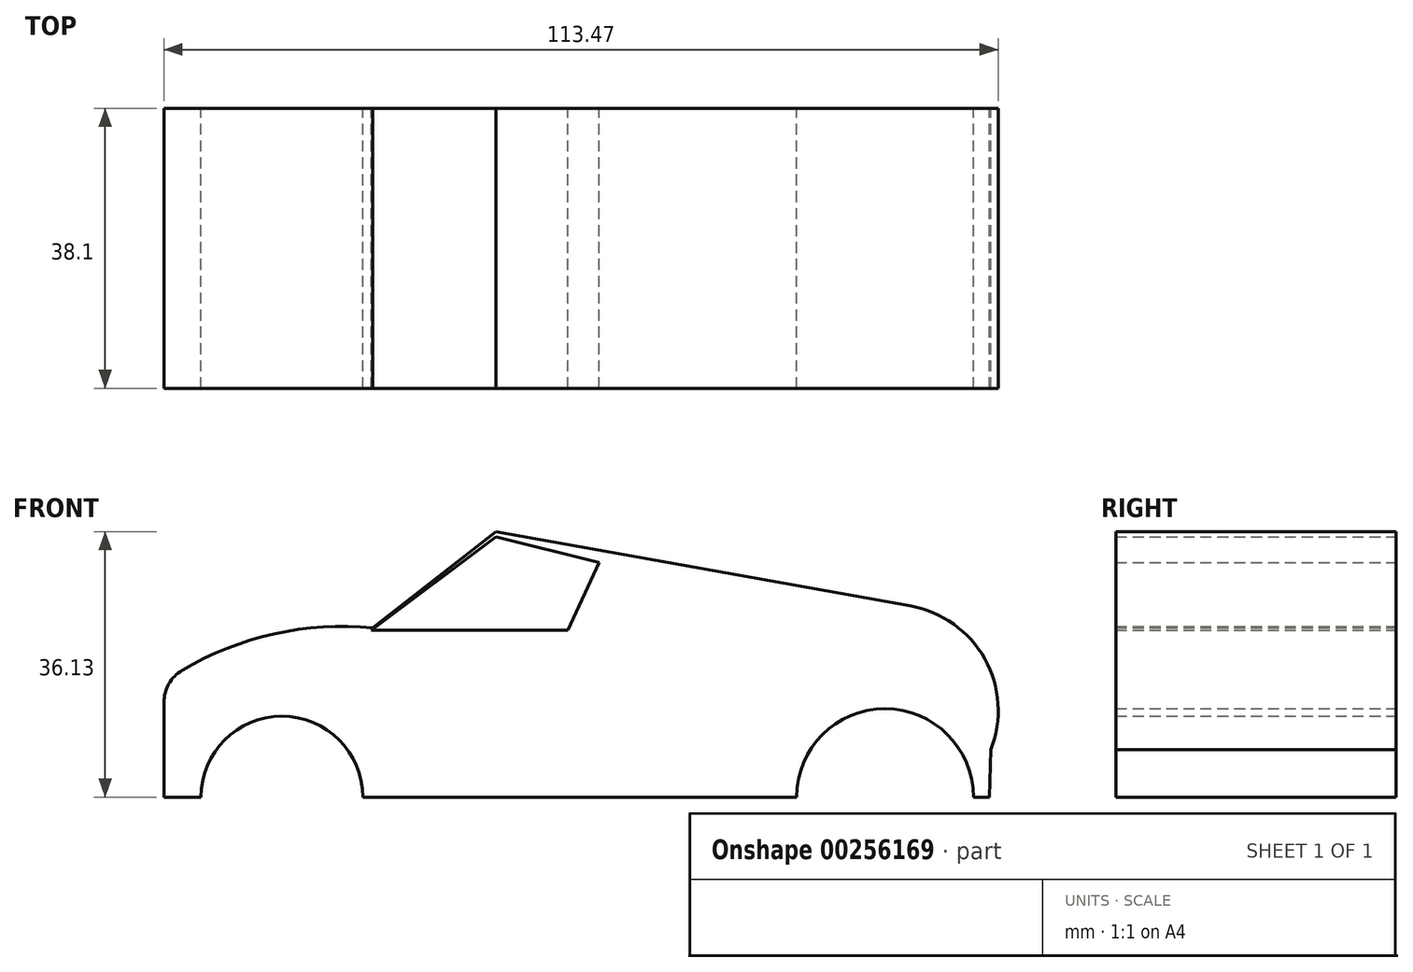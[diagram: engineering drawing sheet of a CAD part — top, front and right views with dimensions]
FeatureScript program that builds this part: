
annotation { "Feature Type Name" : "Feature", "Feature Type Description" : "" }
export const myFeature = defineFeature(function(context is Context, id is Id, definition is map)
    precondition{}
    {
        {
            var Q0;
            Q0=qCreatedBy(makeId("Front.planeOp"),FACE);
            var sketch = newSketch(context, id + "F0", { "sketchPlane" : qUnion([Q0])});
            skLineSegment(sketch, "E0.bottom", {"start": v(-57.89, 0) * mm, "end": v(57.89, 0) * mm});
            skLineSegment(sketch, "E0.top", {"start": v(-57.89, 36.13) * mm, "end": v(57.89, 36.13) * mm});
            skLineSegment(sketch, "E0.left", {"start": v(-57.89, 0) * mm, "end": v(-57.89, 36.13) * mm});
            skLineSegment(sketch, "E0.right", {"start": v(57.89, 0) * mm, "end": v(57.89, 36.13) * mm});
            skPoint(sketch, "E0.middle", {"position": v(0, 18.07) * mm});
            skCircle(sketch, "E1", {"center": v(-41.85, 0) * mm, "radius": 11 * mm});
            skCircle(sketch, "E2", {"center": v(40.19, 0) * mm, "radius": 12.02 * mm});
            skArc(sketch, "E3", {"start": v(-29.5, 23.04) * mm, "mid": v(-44.34, 21.85) * mm, "end": v(-57.89, 15.67) * mm});
            skLineSegment(sketch, "E4", {"start": v(-29.5, 23.04) * mm, "end": v(-12.72, 36.13) * mm});
            skLineSegment(sketch, "E5", {"start": v(-12.72, 36.13) * mm, "end": v(43.7, 26) * mm});
            skArc(sketch, "E6", {"start": v(54.57, 6.45) * mm, "mid": v(53.76, 18.8) * mm, "end": v(43.7, 26) * mm});
            skLineSegment(sketch, "E7", {"start": v(-57.89, 0) * mm, "end": v(54.38, 0) * mm});
            skLineSegment(sketch, "E8", {"start": v(54.38, 0) * mm, "end": v(54.57, 6.45) * mm});
            skSolve(sketch);
        }
        {
            var Q0;
            Q0=qCreatedBy(makeId("Front.planeOp"),FACE);
            var sketch = newSketch(context, id + "F1", { "sketchPlane" : qUnion([Q0])});
            skLineSegment(sketch, "E9", {"start": v(-29.68, 22.68) * mm, "end": v(-2.95, 22.68) * mm});
            skLineSegment(sketch, "E10", {"start": v(-2.95, 22.68) * mm, "end": v(1.3, 31.9) * mm});
            skLineSegment(sketch, "E11", {"start": v(1.3, 31.9) * mm, "end": v(-12.72, 35.4) * mm});
            skLineSegment(sketch, "E12", {"start": v(-12.72, 35.4) * mm, "end": v(-29.68, 22.68) * mm});
            skSolve(sketch);
        }
        {
            var Q0;
            Q0 = qSketchRegion(id + "F1", true);
            var Q1;
            {var subQ10=sQuery(id+"F0.wireOp",EDGE,"E3");Q1=makeQuery(id+"F0.imprint","IMPRINT",FACE,{"disambiguationData":[TD([[makeQuery(id+"F0.imprint","IMPRINT",EDGE,{"derivedFrom":subQ10}),1.0]])]});}
            extrude(context, id + "F2", {"entities" : qUnion([Q0, Q1]), "endBound" : BoundingType.SYMMETRIC, "depth" : 38.1 * mm});
        }
        {
            var Q0;
            Q0=makeQuery(id+"F2.opExtrude","SWEPT_EDGE",EDGE,{"disambiguationData":[OSD([sQuery(id+"F0.wireOp",EDGE,"E5"),sQuery(id+"F0.wireOp",EDGE,"E6")])]});
            var Q1;
            Q1=makeQuery(id+"F2.opExtrude","SWEPT_EDGE",EDGE,{"disambiguationData":[OSD([sQuery(id+"F0.wireOp",EDGE,"E0.left"),sQuery(id+"F0.wireOp",EDGE,"E3")])]});
            fillet(context, id + "F3", {"entities" : qUnion([Q0, Q1]), "radius" : 5.08 * mm, "tangentPropagation" : true, "allowEdgeOverflow" : false});
        }
    });
